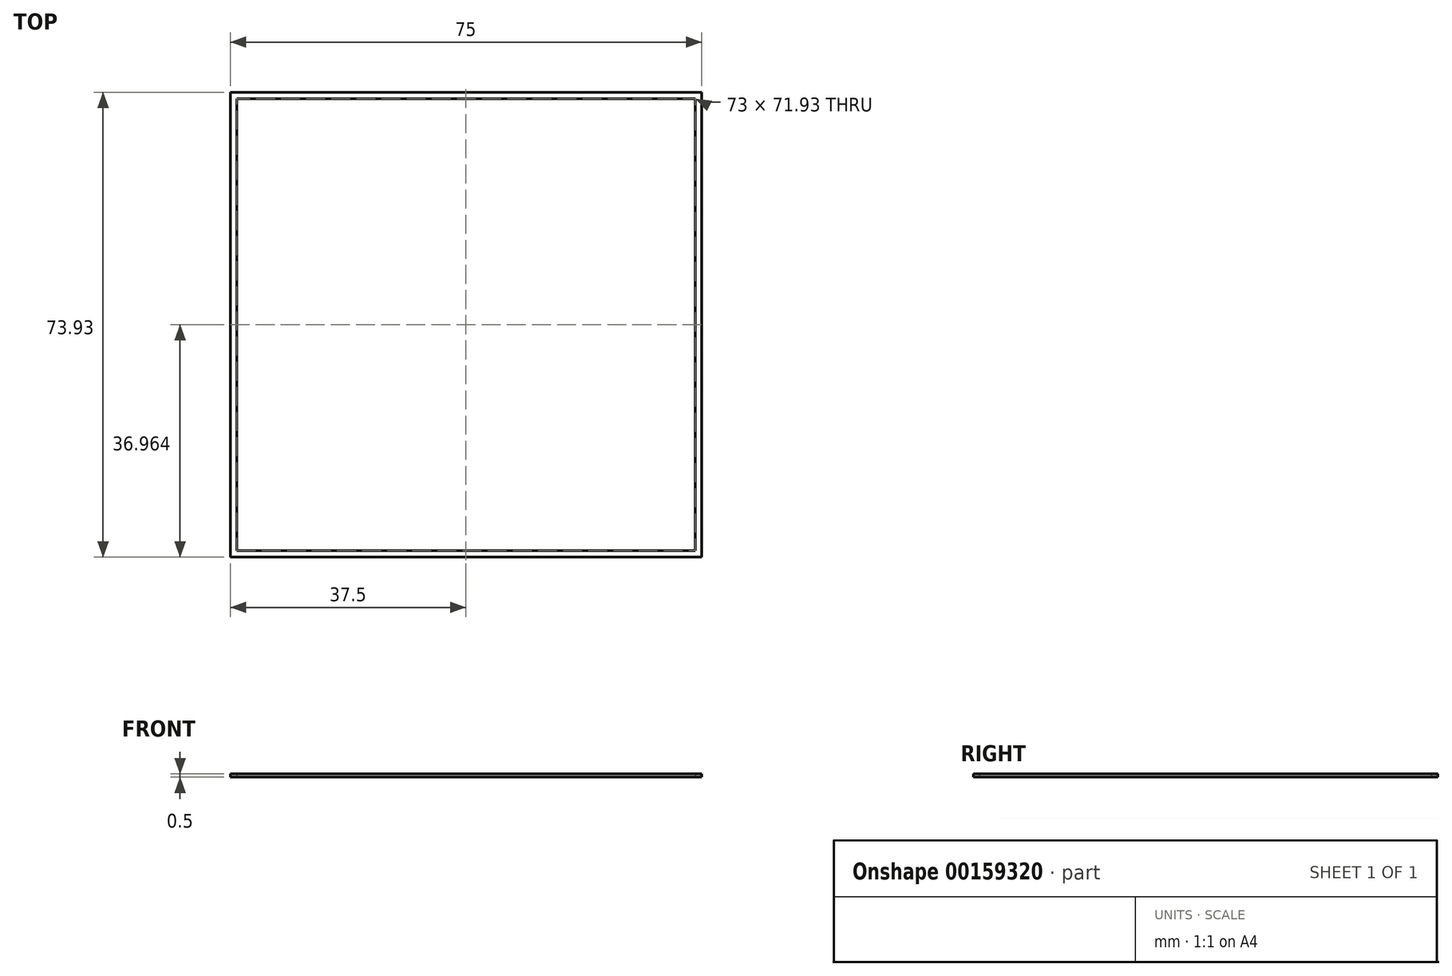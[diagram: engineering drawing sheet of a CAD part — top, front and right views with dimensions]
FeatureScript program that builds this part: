
annotation { "Feature Type Name" : "Feature", "Feature Type Description" : "" }
export const myFeature = defineFeature(function(context is Context, id is Id, definition is map)
    precondition{}
    {
        {
            var Q0;
            Q0=qCreatedBy(makeId("Top.planeOp"),FACE);
            var sketch = newSketch(context, id + "F0", { "sketchPlane" : qUnion([Q0])});
            skLineSegment(sketch, "E0.bottom", {"start": v(-37.5, 36.43) * mm, "end": v(37.5, 36.43) * mm});
            skLineSegment(sketch, "E0.top", {"start": v(-37.5, -37.5) * mm, "end": v(37.5, -37.5) * mm});
            skLineSegment(sketch, "E0.left", {"start": v(-37.5, 36.43) * mm, "end": v(-37.5, -37.5) * mm});
            skLineSegment(sketch, "E0.right", {"start": v(37.5, 36.43) * mm, "end": v(37.5, -37.5) * mm});
            skLineSegment(sketch, "E1.0", {"start": v(-36.5, 35.43) * mm, "end": v(36.5, 35.43) * mm});
            skLineSegment(sketch, "E1.1", {"start": v(-36.5, 35.43) * mm, "end": v(-36.5, -36.5) * mm});
            skLineSegment(sketch, "E1.2", {"start": v(-36.5, -36.5) * mm, "end": v(36.5, -36.5) * mm});
            skLineSegment(sketch, "E1.3", {"start": v(36.5, 35.43) * mm, "end": v(36.5, -36.5) * mm});
            skSolve(sketch);
        }
        {
            var Q0;
            Q0=makeQuery(id+"F0.imprint","IMPRINT",FACE,{"disambiguationData":[TD([[makeQuery(id+"F0.imprint","IMPRINT",EDGE,{"derivedFrom":sQuery(id+"F0.wireOp",EDGE,"E0.bottom")}),-1.0]])]});
            var Q1;
            Q1=sQuery(id+"F0.wireOp",EDGE,"E1.1");
            var Q2;
            Q2=sQuery(id+"F0.wireOp",EDGE,"E0.bottom");
            var Q3;
            Q3=sQuery(id+"F0.wireOp",EDGE,"E1.0");
            var Q4;
            Q4=sQuery(id+"F0.wireOp",EDGE,"E1.3");
            var Q5;
            Q5=sQuery(id+"F0.wireOp",EDGE,"E0.right");
            var Q6;
            Q6=sQuery(id+"F0.wireOp",EDGE,"E1.2");
            var Q7;
            Q7=sQuery(id+"F0.wireOp",EDGE,"E0.top");
            var Q8;
            Q8=sQuery(id+"F0.wireOp",EDGE,"E0.left");
            extrude(context, id + "F1", {"entities" : qUnion([Q0]), "surfaceEntities" : qUnion([Q1, Q2, Q3, Q4, Q5, Q6, Q7, Q8]), "depth" : 0.5 * mm});
        }
    });
